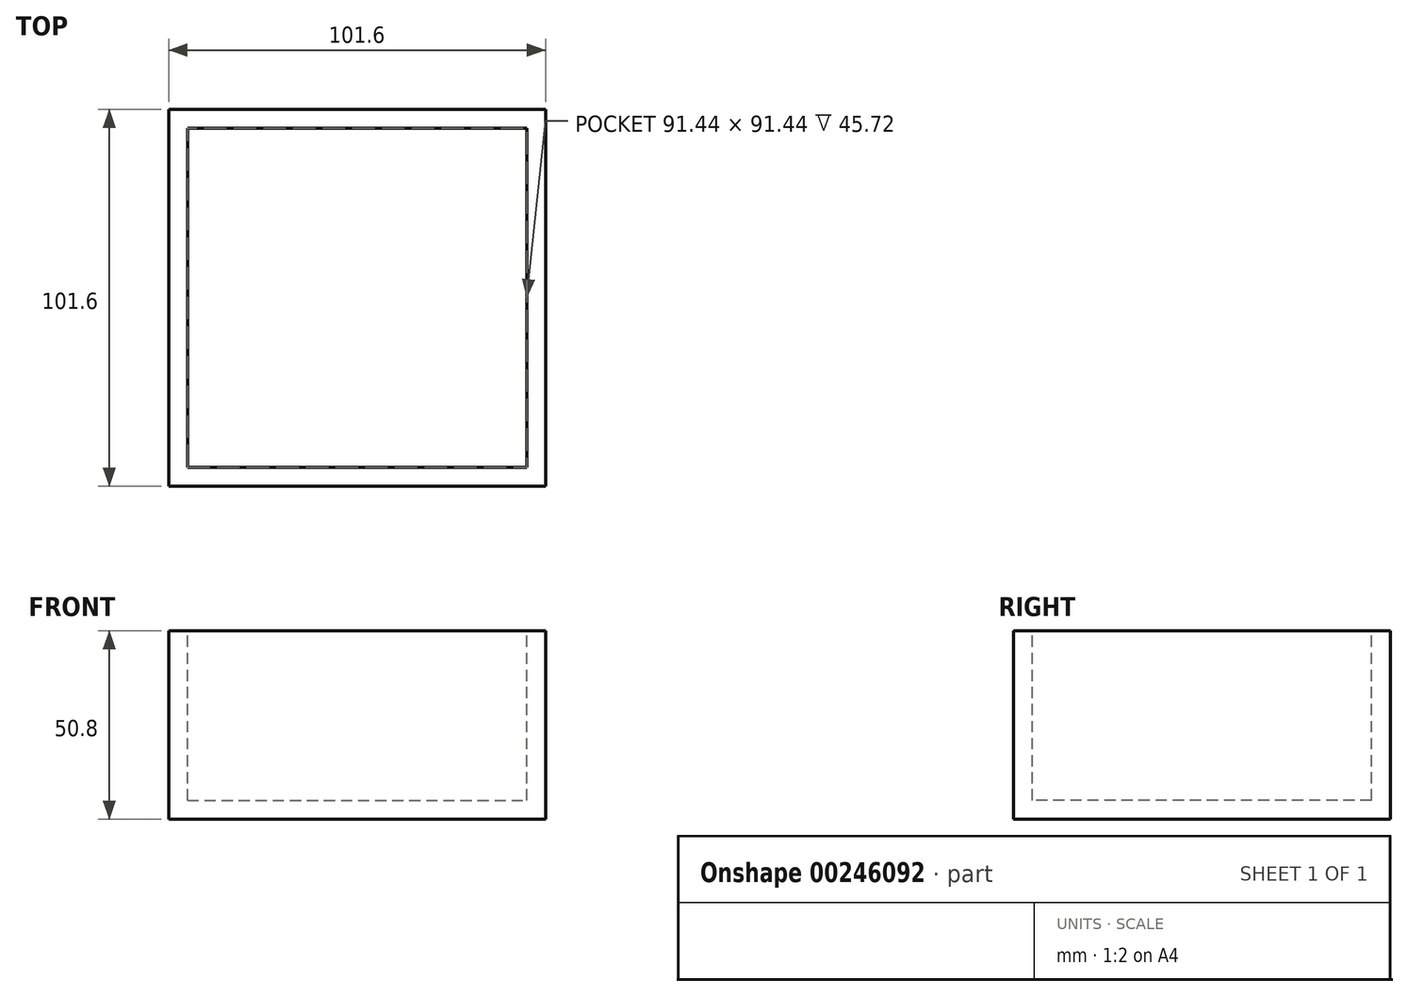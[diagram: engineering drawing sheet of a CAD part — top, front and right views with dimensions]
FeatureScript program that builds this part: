
annotation { "Feature Type Name" : "Feature", "Feature Type Description" : "" }
export const myFeature = defineFeature(function(context is Context, id is Id, definition is map)
    precondition{}
    {
        {
            var Q0;
            Q0=qCreatedBy(makeId("Front.planeOp"),FACE);
            var sketch = newSketch(context, id + "F0", { "sketchPlane" : qUnion([Q0])});
            skLineSegment(sketch, "E0", {"start": v(0, 0) * mm, "end": v(-50.8, 0) * mm});
            skLineSegment(sketch, "E1", {"start": v(-50.8, 0) * mm, "end": v(-50.8, 50.8) * mm});
            skLineSegment(sketch, "E2", {"start": v(50.8, 50.8) * mm, "end": v(50.8, 0) * mm});
            skLineSegment(sketch, "E3", {"start": v(50.8, 0) * mm, "end": v(0, 0) * mm});
            skLineSegment(sketch, "E4", {"start": v(-50.8, 50.8) * mm, "end": v(0, 50.8) * mm});
            skLineSegment(sketch, "E5", {"start": v(0, 50.8) * mm, "end": v(50.8, 50.8) * mm});
            skSolve(sketch);
        }
        {
            var Q0;
            Q0=makeQuery(id+"F0.imprint","IMPRINT",FACE,{"disambiguationData":[TD([[makeQuery(id+"F0.imprint","IMPRINT",EDGE,{"derivedFrom":sQuery(id+"F0.wireOp",EDGE,"E0")}),-1.0]])]});
            extrude(context, id + "F1", {"entities" : qUnion([Q0]), "depth" : 101.6 * mm});
        }
        {
            var Q0;
            Q0=makeQuery(id+"F1.opExtrude","SWEPT_FACE",FACE,{"disambiguationData":[OSD([sQuery(id+"F0.wireOp",EDGE,"E4"),sQuery(id+"F0.wireOp",EDGE,"E5")])]});
            var sketch = newSketch(context, id + "F2", { "sketchPlane" : qUnion([Q0])});
            skLineSegment(sketch, "E6", {"start": v(-45.72, -5.08) * mm, "end": v(-45.72, -96.52) * mm});
            skLineSegment(sketch, "E7", {"start": v(-45.72, -96.52) * mm, "end": v(45.72, -96.52) * mm});
            skLineSegment(sketch, "E8", {"start": v(45.72, -96.52) * mm, "end": v(45.72, -5.08) * mm});
            skLineSegment(sketch, "E9", {"start": v(-45.72, -5.08) * mm, "end": v(45.72, -5.08) * mm});
            skSolve(sketch);
        }
        {
            var Q0;
            Q0=makeQuery(id+"F2.imprint","IMPRINT",FACE,{"disambiguationData":[TD([[makeQuery(id+"F2.imprint","IMPRINT",EDGE,{"derivedFrom":sQuery(id+"F2.wireOp",EDGE,"E6")}),1.0]])]});
            extrude(context, id + "F3", {"entities" : qUnion([Q0]), "operationType" : NewBodyOperationType.REMOVE, "oppositeDirection" : true, "depth" : 45.72 * mm});
        }
    });
